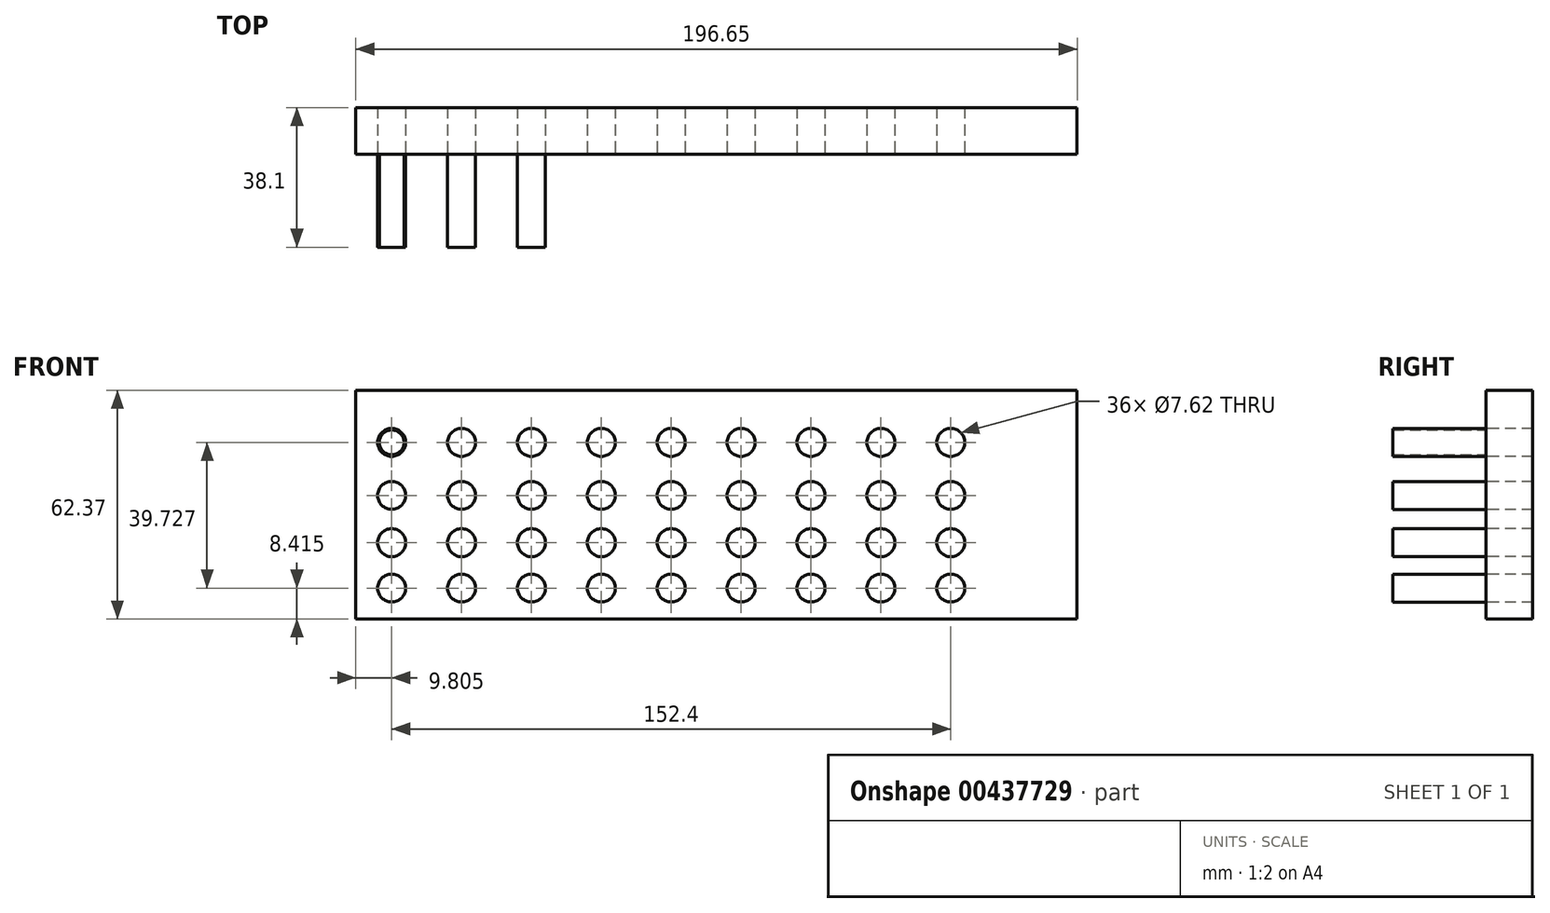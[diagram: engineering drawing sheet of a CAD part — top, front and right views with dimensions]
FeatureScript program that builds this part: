
annotation { "Feature Type Name" : "Feature", "Feature Type Description" : "" }
export const myFeature = defineFeature(function(context is Context, id is Id, definition is map)
    precondition{}
    {
        {
            var Q0;
            Q0=qCreatedBy(makeId("Front.planeOp"),FACE);
            var sketch = newSketch(context, id + "F0", { "sketchPlane" : qUnion([Q0])});
            skLineSegment(sketch, "E0.bottom", {"start": v(-98.94, 33.84) * mm, "end": v(97.7, 33.84) * mm});
            skLineSegment(sketch, "E0.top", {"start": v(-98.94, -28.53) * mm, "end": v(97.7, -28.53) * mm});
            skLineSegment(sketch, "E0.left", {"start": v(-98.94, 33.84) * mm, "end": v(-98.94, -28.53) * mm});
            skLineSegment(sketch, "E0.right", {"start": v(97.7, 33.84) * mm, "end": v(97.7, -28.53) * mm});
            skSolve(sketch);
        }
        {
            var Q0;
            Q0=makeQuery(id+"F0.imprint","IMPRINT",FACE,{"disambiguationData":[TD([[makeQuery(id+"F0.imprint","IMPRINT",EDGE,{"derivedFrom":sQuery(id+"F0.wireOp",EDGE,"E0.bottom")}),-1.0]])]});
            var sketch = newSketch(context, id + "F1", { "sketchPlane" : qUnion([Q0])});
            skCircle(sketch, "E1", {"center": v(-89.13, -20.12) * mm, "radius": 3.81 * mm});
            skCircle(sketch, "E2.1.0.0", {"center": v(-70.08, -20.12) * mm, "radius": 3.81 * mm});
            skCircle(sketch, "E2.2.0.0", {"center": v(-51.03, -20.12) * mm, "radius": 3.81 * mm});
            skCircle(sketch, "E2.3.0.0", {"center": v(-31.98, -20.12) * mm, "radius": 3.81 * mm});
            skCircle(sketch, "E2.4.0.0", {"center": v(-12.93, -20.12) * mm, "radius": 3.81 * mm});
            skCircle(sketch, "E2.5.0.0", {"center": v(6.12, -20.12) * mm, "radius": 3.81 * mm});
            skCircle(sketch, "E2.6.0.0", {"center": v(25.17, -20.12) * mm, "radius": 3.81 * mm});
            skCircle(sketch, "E2.7.0.0", {"center": v(44.22, -20.12) * mm, "radius": 3.81 * mm});
            skLineSegment(sketch, "E2.direction1", {"start": v(-89.13, -20.12) * mm, "end": v(-70.08, -20.12) * mm, "construction": true});
            skCircle(sketch, "E3.0.8.0", {"center": v(63.27, -20.12) * mm, "radius": 3.81 * mm});
            skCircle(sketch, "E4", {"center": v(-89.13, -7.73) * mm, "radius": 3.81 * mm});
            skCircle(sketch, "E5.1.0.0", {"center": v(-70.08, -7.73) * mm, "radius": 3.81 * mm});
            skCircle(sketch, "E5.2.0.0", {"center": v(-51.03, -7.73) * mm, "radius": 3.81 * mm});
            skCircle(sketch, "E5.3.0.0", {"center": v(-31.98, -7.73) * mm, "radius": 3.81 * mm});
            skCircle(sketch, "E5.4.0.0", {"center": v(-12.93, -7.73) * mm, "radius": 3.81 * mm});
            skCircle(sketch, "E5.5.0.0", {"center": v(6.12, -7.73) * mm, "radius": 3.81 * mm});
            skCircle(sketch, "E5.6.0.0", {"center": v(25.17, -7.73) * mm, "radius": 3.81 * mm});
            skCircle(sketch, "E5.7.0.0", {"center": v(44.22, -7.73) * mm, "radius": 3.81 * mm});
            skLineSegment(sketch, "E5.direction1", {"start": v(-89.13, -7.73) * mm, "end": v(-70.08, -7.73) * mm, "construction": true});
            skCircle(sketch, "E6.0.8.0", {"center": v(63.27, -7.73) * mm, "radius": 3.81 * mm});
            skCircle(sketch, "E7", {"center": v(-89.13, 5.17) * mm, "radius": 3.81 * mm});
            skCircle(sketch, "E8.1.0.0", {"center": v(-70.08, 5.17) * mm, "radius": 3.81 * mm});
            skCircle(sketch, "E8.2.0.0", {"center": v(-51.03, 5.17) * mm, "radius": 3.81 * mm});
            skCircle(sketch, "E8.3.0.0", {"center": v(-31.98, 5.17) * mm, "radius": 3.81 * mm});
            skCircle(sketch, "E8.4.0.0", {"center": v(-12.93, 5.17) * mm, "radius": 3.81 * mm});
            skCircle(sketch, "E8.5.0.0", {"center": v(6.12, 5.17) * mm, "radius": 3.81 * mm});
            skCircle(sketch, "E8.6.0.0", {"center": v(25.17, 5.17) * mm, "radius": 3.81 * mm});
            skCircle(sketch, "E8.7.0.0", {"center": v(44.22, 5.17) * mm, "radius": 3.81 * mm});
            skLineSegment(sketch, "E8.direction1", {"start": v(-89.13, 5.17) * mm, "end": v(-70.08, 5.17) * mm, "construction": true});
            skCircle(sketch, "E9.0.8.0", {"center": v(63.27, 5.17) * mm, "radius": 3.81 * mm});
            skCircle(sketch, "E10", {"center": v(-89.13, 19.61) * mm, "radius": 3.81 * mm});
            skCircle(sketch, "E11.1.0.0", {"center": v(-70.08, 19.61) * mm, "radius": 3.81 * mm});
            skCircle(sketch, "E11.2.0.0", {"center": v(-51.03, 19.61) * mm, "radius": 3.81 * mm});
            skCircle(sketch, "E11.3.0.0", {"center": v(-31.98, 19.61) * mm, "radius": 3.81 * mm});
            skCircle(sketch, "E11.4.0.0", {"center": v(-12.93, 19.61) * mm, "radius": 3.81 * mm});
            skCircle(sketch, "E11.5.0.0", {"center": v(6.12, 19.61) * mm, "radius": 3.81 * mm});
            skCircle(sketch, "E11.6.0.0", {"center": v(25.17, 19.61) * mm, "radius": 3.81 * mm});
            skCircle(sketch, "E11.7.0.0", {"center": v(44.22, 19.61) * mm, "radius": 3.81 * mm});
            skLineSegment(sketch, "E11.direction1", {"start": v(-89.13, 19.61) * mm, "end": v(-70.08, 19.61) * mm, "construction": true});
            skCircle(sketch, "E12.0.8.0", {"center": v(63.27, 19.61) * mm, "radius": 3.81 * mm});
            skSolve(sketch);
        }
        {
            var Q0;
            Q0=makeQuery(id+"F1.imprint","IMPRINT",FACE,{"disambiguationData":[TD([[makeQuery(id+"F1.imprint","IMPRINT",EDGE,{"derivedFrom":sQuery(id+"F1.wireOp",EDGE,"E1")}),-1.0]])]});
            extrude(context, id + "F2", {"entities" : qUnion([Q0]), "oppositeDirection" : true, "depth" : 12.7 * mm});
        }
        {
            var Q0;
            Q0=makeQuery(id+"F2.opExtrude","CAP_FACE",FACE,{"disambiguationData":[OSD([sQuery(id+"F0.wireOp",EDGE,"E0.bottom"),sQuery(id+"F0.wireOp",EDGE,"E0.top"),sQuery(id+"F0.wireOp",EDGE,"E0.left"),sQuery(id+"F0.wireOp",EDGE,"E0.right"),sQuery(id+"F1.wireOp",EDGE,"E1"),sQuery(id+"F1.wireOp",EDGE,"E2.1.0.0"),sQuery(id+"F1.wireOp",EDGE,"E2.2.0.0"),sQuery(id+"F1.wireOp",EDGE,"E2.3.0.0"),sQuery(id+"F1.wireOp",EDGE,"E2.4.0.0"),sQuery(id+"F1.wireOp",EDGE,"E2.5.0.0"),sQuery(id+"F1.wireOp",EDGE,"E2.6.0.0"),sQuery(id+"F1.wireOp",EDGE,"E2.7.0.0"),sQuery(id+"F1.wireOp",EDGE,"E3.0.8.0"),sQuery(id+"F1.wireOp",EDGE,"E4"),sQuery(id+"F1.wireOp",EDGE,"E5.1.0.0"),sQuery(id+"F1.wireOp",EDGE,"E5.2.0.0"),sQuery(id+"F1.wireOp",EDGE,"E5.3.0.0"),sQuery(id+"F1.wireOp",EDGE,"E5.4.0.0"),sQuery(id+"F1.wireOp",EDGE,"E5.5.0.0"),sQuery(id+"F1.wireOp",EDGE,"E5.6.0.0"),sQuery(id+"F1.wireOp",EDGE,"E5.7.0.0"),sQuery(id+"F1.wireOp",EDGE,"E6.0.8.0"),sQuery(id+"F1.wireOp",EDGE,"E7"),sQuery(id+"F1.wireOp",EDGE,"E8.1.0.0"),sQuery(id+"F1.wireOp",EDGE,"E8.2.0.0"),sQuery(id+"F1.wireOp",EDGE,"E8.3.0.0"),sQuery(id+"F1.wireOp",EDGE,"E8.4.0.0"),sQuery(id+"F1.wireOp",EDGE,"E8.5.0.0"),sQuery(id+"F1.wireOp",EDGE,"E8.6.0.0"),sQuery(id+"F1.wireOp",EDGE,"E8.7.0.0"),sQuery(id+"F1.wireOp",EDGE,"E9.0.8.0"),sQuery(id+"F1.wireOp",EDGE,"E10"),sQuery(id+"F1.wireOp",EDGE,"E11.1.0.0"),sQuery(id+"F1.wireOp",EDGE,"E11.2.0.0"),sQuery(id+"F1.wireOp",EDGE,"E11.3.0.0"),sQuery(id+"F1.wireOp",EDGE,"E11.4.0.0"),sQuery(id+"F1.wireOp",EDGE,"E11.5.0.0"),sQuery(id+"F1.wireOp",EDGE,"E11.6.0.0"),sQuery(id+"F1.wireOp",EDGE,"E11.7.0.0"),sQuery(id+"F1.wireOp",EDGE,"E12.0.8.0")])],"isStart":true});
            var sketch = newSketch(context, id + "F3", { "sketchPlane" : qUnion([Q0])});
            skCircle(sketch, "E13", {"center": v(-89.13, 19.61) * mm, "radius": 3.38 * mm});
            skSolve(sketch);
        }
        {
            var Q0;
            Q0 = qSketchRegion(id + "F3", true);
            extrude(context, id + "F4", {"entities" : qUnion([Q0]), "depth" : 25.4 * mm});
        }
        {
            var Q0;
            Q0=makeQuery(id+"F2.opExtrude","CAP_FACE",FACE,{"disambiguationData":[OSD([sQuery(id+"F0.wireOp",EDGE,"E0.bottom"),sQuery(id+"F0.wireOp",EDGE,"E0.top"),sQuery(id+"F0.wireOp",EDGE,"E0.left"),sQuery(id+"F0.wireOp",EDGE,"E0.right"),sQuery(id+"F1.wireOp",EDGE,"E1"),sQuery(id+"F1.wireOp",EDGE,"E2.1.0.0"),sQuery(id+"F1.wireOp",EDGE,"E2.2.0.0"),sQuery(id+"F1.wireOp",EDGE,"E2.3.0.0"),sQuery(id+"F1.wireOp",EDGE,"E2.4.0.0"),sQuery(id+"F1.wireOp",EDGE,"E2.5.0.0"),sQuery(id+"F1.wireOp",EDGE,"E2.6.0.0"),sQuery(id+"F1.wireOp",EDGE,"E2.7.0.0"),sQuery(id+"F1.wireOp",EDGE,"E3.0.8.0"),sQuery(id+"F1.wireOp",EDGE,"E4"),sQuery(id+"F1.wireOp",EDGE,"E5.1.0.0"),sQuery(id+"F1.wireOp",EDGE,"E5.2.0.0"),sQuery(id+"F1.wireOp",EDGE,"E5.3.0.0"),sQuery(id+"F1.wireOp",EDGE,"E5.4.0.0"),sQuery(id+"F1.wireOp",EDGE,"E5.5.0.0"),sQuery(id+"F1.wireOp",EDGE,"E5.6.0.0"),sQuery(id+"F1.wireOp",EDGE,"E5.7.0.0"),sQuery(id+"F1.wireOp",EDGE,"E6.0.8.0"),sQuery(id+"F1.wireOp",EDGE,"E7"),sQuery(id+"F1.wireOp",EDGE,"E8.1.0.0"),sQuery(id+"F1.wireOp",EDGE,"E8.2.0.0"),sQuery(id+"F1.wireOp",EDGE,"E8.3.0.0"),sQuery(id+"F1.wireOp",EDGE,"E8.4.0.0"),sQuery(id+"F1.wireOp",EDGE,"E8.5.0.0"),sQuery(id+"F1.wireOp",EDGE,"E8.6.0.0"),sQuery(id+"F1.wireOp",EDGE,"E8.7.0.0"),sQuery(id+"F1.wireOp",EDGE,"E9.0.8.0"),sQuery(id+"F1.wireOp",EDGE,"E10"),sQuery(id+"F1.wireOp",EDGE,"E11.1.0.0"),sQuery(id+"F1.wireOp",EDGE,"E11.2.0.0"),sQuery(id+"F1.wireOp",EDGE,"E11.3.0.0"),sQuery(id+"F1.wireOp",EDGE,"E11.4.0.0"),sQuery(id+"F1.wireOp",EDGE,"E11.5.0.0"),sQuery(id+"F1.wireOp",EDGE,"E11.6.0.0"),sQuery(id+"F1.wireOp",EDGE,"E11.7.0.0"),sQuery(id+"F1.wireOp",EDGE,"E12.0.8.0")])],"isStart":true});
            var sketch = newSketch(context, id + "F5", { "sketchPlane" : qUnion([Q0])});
            skSolve(sketch);
        }
        {
            var Q0;
            Q0=makeQuery(id+"F5.imprint","IMPRINT",FACE,{"disambiguationData":[TD([[makeQuery(id+"F5.imprint","IMPRINT",EDGE,{"derivedFrom":makeQuery(id+"F2.opExtrude","CAP_EDGE",EDGE,{"disambiguationData":[OSD([sQuery(id+"F1.wireOp",EDGE,"E7")])],"isStart":true})}),1.0]])]});
            var Q1;
            Q1=makeQuery(id+"F5.imprint","IMPRINT",FACE,{"disambiguationData":[TD([[makeQuery(id+"F5.imprint","IMPRINT",EDGE,{"derivedFrom":makeQuery(id+"F2.opExtrude","CAP_EDGE",EDGE,{"disambiguationData":[OSD([sQuery(id+"F1.wireOp",EDGE,"E4")])],"isStart":true})}),1.0]])]});
            var Q2;
            Q2=makeQuery(id+"F5.imprint","IMPRINT",FACE,{"disambiguationData":[TD([[makeQuery(id+"F5.imprint","IMPRINT",EDGE,{"derivedFrom":makeQuery(id+"F2.opExtrude","CAP_EDGE",EDGE,{"disambiguationData":[OSD([sQuery(id+"F1.wireOp",EDGE,"E1")])],"isStart":true})}),1.0]])]});
            var Q3;
            Q3=makeQuery(id+"F5.imprint","IMPRINT",FACE,{"disambiguationData":[TD([[makeQuery(id+"F5.imprint","IMPRINT",EDGE,{"derivedFrom":makeQuery(id+"F2.opExtrude","CAP_EDGE",EDGE,{"disambiguationData":[OSD([sQuery(id+"F1.wireOp",EDGE,"E11.1.0.0")])],"isStart":true})}),1.0]])]});
            var Q4;
            Q4=makeQuery(id+"F5.imprint","IMPRINT",FACE,{"disambiguationData":[TD([[makeQuery(id+"F5.imprint","IMPRINT",EDGE,{"derivedFrom":makeQuery(id+"F2.opExtrude","CAP_EDGE",EDGE,{"disambiguationData":[OSD([sQuery(id+"F1.wireOp",EDGE,"E8.1.0.0")])],"isStart":true})}),1.0]])]});
            var Q5;
            Q5=makeQuery(id+"F5.imprint","IMPRINT",FACE,{"disambiguationData":[TD([[makeQuery(id+"F5.imprint","IMPRINT",EDGE,{"derivedFrom":makeQuery(id+"F2.opExtrude","CAP_EDGE",EDGE,{"disambiguationData":[OSD([sQuery(id+"F1.wireOp",EDGE,"E5.1.0.0")])],"isStart":true})}),1.0]])]});
            var Q6;
            Q6=makeQuery(id+"F5.imprint","IMPRINT",FACE,{"disambiguationData":[TD([[makeQuery(id+"F5.imprint","IMPRINT",EDGE,{"derivedFrom":makeQuery(id+"F2.opExtrude","CAP_EDGE",EDGE,{"disambiguationData":[OSD([sQuery(id+"F1.wireOp",EDGE,"E2.1.0.0")])],"isStart":true})}),1.0]])]});
            var Q7;
            Q7=makeQuery(id+"F5.imprint","IMPRINT",FACE,{"disambiguationData":[TD([[makeQuery(id+"F5.imprint","IMPRINT",EDGE,{"derivedFrom":makeQuery(id+"F2.opExtrude","CAP_EDGE",EDGE,{"disambiguationData":[OSD([sQuery(id+"F1.wireOp",EDGE,"E11.2.0.0")])],"isStart":true})}),1.0]])]});
            var Q8;
            Q8=makeQuery(id+"F5.imprint","IMPRINT",FACE,{"disambiguationData":[TD([[makeQuery(id+"F5.imprint","IMPRINT",EDGE,{"derivedFrom":makeQuery(id+"F2.opExtrude","CAP_EDGE",EDGE,{"disambiguationData":[OSD([sQuery(id+"F1.wireOp",EDGE,"E8.2.0.0")])],"isStart":true})}),1.0]])]});
            var Q9;
            Q9=makeQuery(id+"F5.imprint","IMPRINT",FACE,{"disambiguationData":[TD([[makeQuery(id+"F5.imprint","IMPRINT",EDGE,{"derivedFrom":makeQuery(id+"F2.opExtrude","CAP_EDGE",EDGE,{"disambiguationData":[OSD([sQuery(id+"F1.wireOp",EDGE,"E5.2.0.0")])],"isStart":true})}),1.0]])]});
            var Q10;
            Q10=makeQuery(id+"F5.imprint","IMPRINT",FACE,{"disambiguationData":[TD([[makeQuery(id+"F5.imprint","IMPRINT",EDGE,{"derivedFrom":makeQuery(id+"F2.opExtrude","CAP_EDGE",EDGE,{"disambiguationData":[OSD([sQuery(id+"F1.wireOp",EDGE,"E2.2.0.0")])],"isStart":true})}),1.0]])]});
            extrude(context, id + "F6", {"entities" : qUnion([Q0, Q1, Q2, Q3, Q4, Q5, Q6, Q7, Q8, Q9, Q10]), "depth" : 25.4 * mm});
        }
    });
